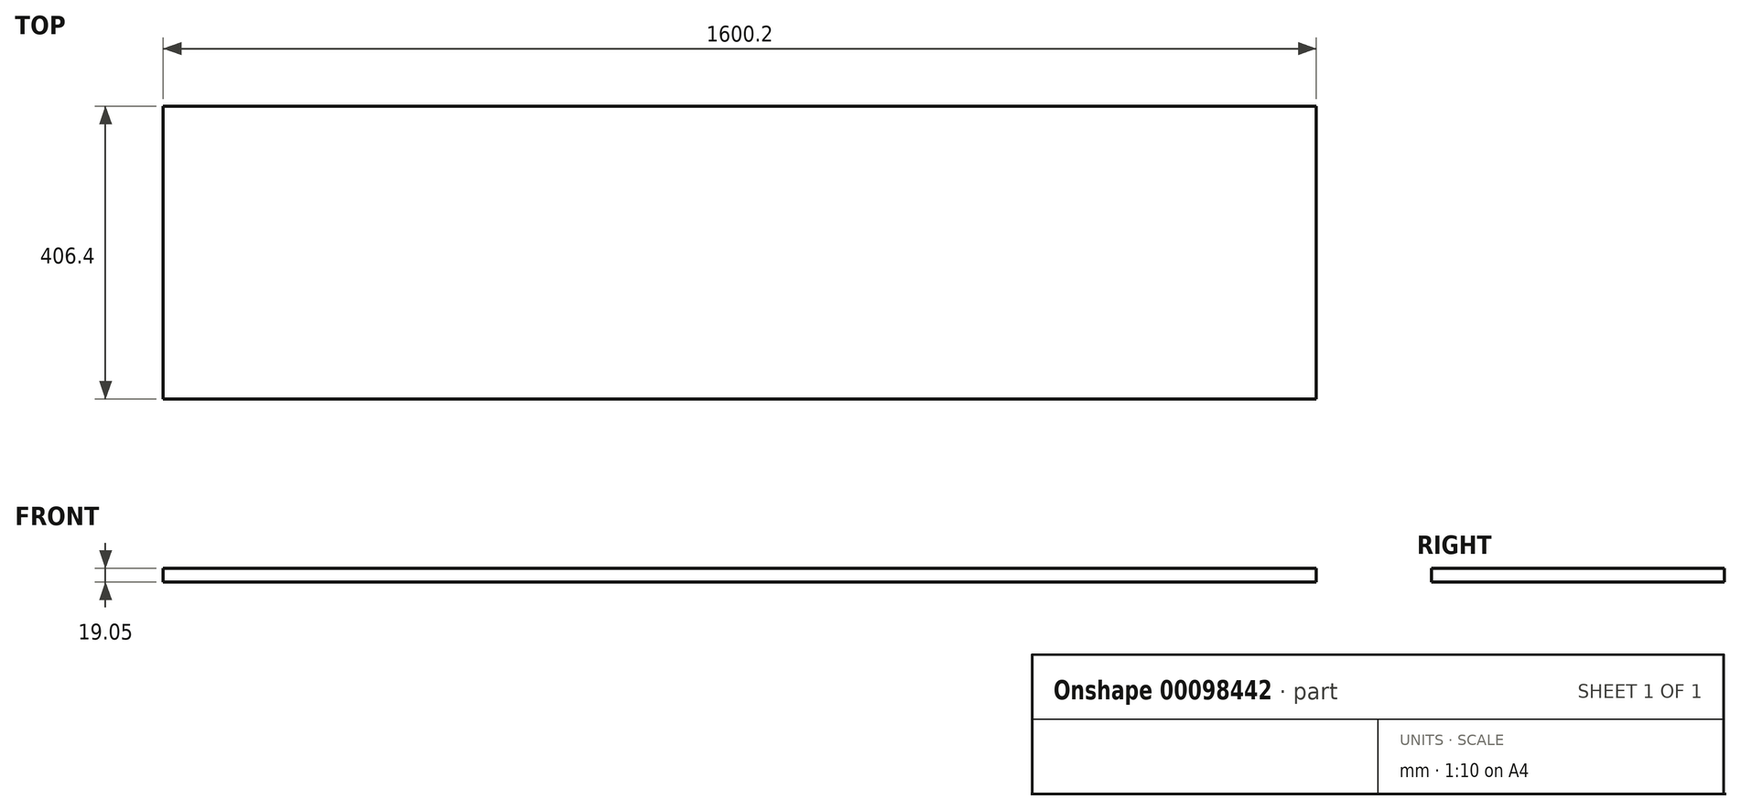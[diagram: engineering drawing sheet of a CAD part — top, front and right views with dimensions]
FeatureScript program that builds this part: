
annotation { "Feature Type Name" : "Feature", "Feature Type Description" : "" }
export const myFeature = defineFeature(function(context is Context, id is Id, definition is map)
    precondition{}
    {
        {
            var Q0;
            Q0=qCreatedBy(makeId("Top.planeOp"),FACE);
            var sketch = newSketch(context, id + "F0", { "sketchPlane" : qUnion([Q0])});
            skLineSegment(sketch, "E0.bottom", {"start": v(-798.47, -772.31) * mm, "end": v(801.73, -772.31) * mm});
            skLineSegment(sketch, "E0.top", {"start": v(-798.47, -365.91) * mm, "end": v(801.73, -365.91) * mm});
            skLineSegment(sketch, "E0.left", {"start": v(-798.47, -772.31) * mm, "end": v(-798.47, -365.91) * mm});
            skLineSegment(sketch, "E0.right", {"start": v(801.73, -772.31) * mm, "end": v(801.73, -365.91) * mm});
            skSolve(sketch);
        }
        {
            var Q0;
            Q0 = qSketchRegion(id + "F0", true);
            extrude(context, id + "F1", {"entities" : qUnion([Q0]), "depth" : 19.05 * mm});
        }
    });
